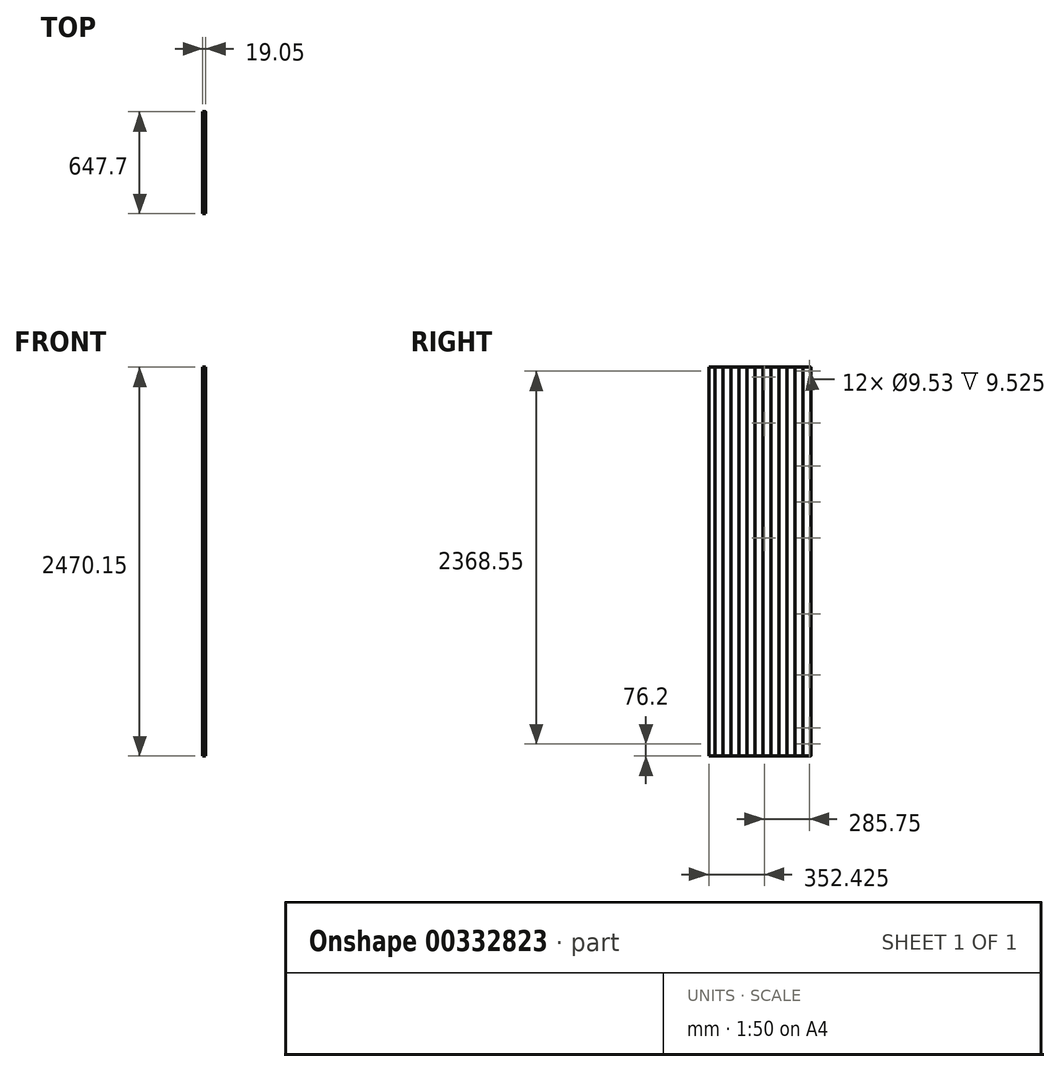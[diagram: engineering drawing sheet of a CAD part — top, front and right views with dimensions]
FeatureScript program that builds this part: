
annotation { "Feature Type Name" : "Feature", "Feature Type Description" : "" }
export const myFeature = defineFeature(function(context is Context, id is Id, definition is map)
    precondition{}
    {
        {
            var Q0;
            Q0=qCreatedBy(makeId("Right.planeOp"),FACE);
            var sketch = newSketch(context, id + "F0", { "sketchPlane" : qUnion([Q0])});
            skLineSegment(sketch, "E0.bottom", {"start": v(0, 0) * mm, "end": v(-647.7, 0) * mm});
            skLineSegment(sketch, "E0.top", {"start": v(0, 2470.15) * mm, "end": v(-647.7, 2470.15) * mm});
            skLineSegment(sketch, "E0.left", {"start": v(0, 0) * mm, "end": v(0, 2470.15) * mm});
            skLineSegment(sketch, "E0.right", {"start": v(-647.7, 0) * mm, "end": v(-647.7, 2470.15) * mm});
            skSolve(sketch);
        }
        {
            var Q0;
            Q0=qSketchRegion(id+"F0",true);
            extrude(context, id + "F1", {"entities" : qUnion([Q0]), "depth" : 19.05 * mm});
        }
        {
            var Q0;
            Q0=qCreatedBy(makeId("Right.planeOp"),FACE);
            cPlane(context, id + "F2", {"entities" : qUnion([Q0]), "cplaneType" : CPlaneType.OFFSET, "offset" : 25.4 * mm, "oppositeDirection" : true, "width" : 152.4 * mm, "height" : 152.4 * mm});
        }
        {
            var Q0;
            Q0=qCreatedBy(id+"F2.planeOp",FACE);
            var sketch = newSketch(context, id + "F3", { "sketchPlane" : qUnion([Q0])});
            skCircle(sketch, "E1", {"center": v(-536.58, 63.5) * mm, "radius": 4.76 * mm, "construction": true});
            skCircle(sketch, "E2", {"center": v(-9.52, 76.2) * mm, "radius": 4.76 * mm});
            skCircle(sketch, "E3", {"center": v(-536.58, 177.8) * mm, "radius": 4.76 * mm, "construction": true});
            skCircle(sketch, "E4", {"center": v(-600.08, 177.8) * mm, "radius": 4.76 * mm, "construction": true});
            skCircle(sketch, "E5", {"center": v(-600.07, 901.7) * mm, "radius": 4.76 * mm, "construction": true});
            skCircle(sketch, "E6", {"center": v(-295.28, 1384.3) * mm, "radius": 4.76 * mm});
            skCircle(sketch, "E7", {"center": v(-295.28, 2114.55) * mm, "radius": 4.76 * mm});
            skCircle(sketch, "E8", {"center": v(-295.28, 2406.65) * mm, "radius": 4.76 * mm});
            skCircle(sketch, "E9", {"center": v(-9.53, 2444.75) * mm, "radius": 4.76 * mm});
            skCircle(sketch, "E10", {"center": v(-9.53, 2114.55) * mm, "radius": 4.76 * mm});
            skCircle(sketch, "E11", {"center": v(-9.53, 1384.3) * mm, "radius": 4.76 * mm});
            skCircle(sketch, "E12", {"center": v(-9.53, 901.7) * mm, "radius": 4.76 * mm});
            skCircle(sketch, "E13", {"center": v(-9.53, 177.8) * mm, "radius": 4.76 * mm});
            skCircle(sketch, "E14", {"center": v(-536.58, 76.2) * mm, "radius": 4.76 * mm, "construction": true});
            skCircle(sketch, "E15", {"center": v(-558.8, 161.93) * mm, "radius": 4.76 * mm, "construction": true});
            skCircle(sketch, "E16", {"center": v(-600.08, 514.35) * mm, "radius": 4.76 * mm, "construction": true});
            skCircle(sketch, "E17", {"center": v(-9.53, 514.35) * mm, "radius": 4.76 * mm});
            skCircle(sketch, "E18", {"center": v(-9.53, 1612.9) * mm, "radius": 4.76 * mm});
            skCircle(sketch, "E19", {"center": v(-9.53, 1841.5) * mm, "radius": 4.76 * mm});
            skSolve(sketch);
        }
        {
            var Q0;
            Q0=qSketchRegion(id+"F3",true);
            extrude(context, id + "F4", {"entities" : qUnion([Q0]), "operationType" : NewBodyOperationType.REMOVE, "depth" : 34.92 * mm});
        }
        {
            var Q0;
            Q0=qCreatedBy(makeId("Top.planeOp"),FACE);
            var sketch = newSketch(context, id + "F5", { "sketchPlane" : qUnion([Q0])});
            skArc(sketch, "E20", {"start": v(19.05, 50.3) * mm, "mid": v(18.9, 50.65) * mm, "end": v(18.54, 50.8) * mm});
            skArc(sketch, "E21", {"start": v(18.54, 50.8) * mm, "mid": v(18.9, 50.95) * mm, "end": v(19.05, 51.3) * mm});
            skArc(sketch, "E22", {"start": v(19.05, 50.3) * mm, "mid": v(19.56, 50.8) * mm, "end": v(19.05, 51.3) * mm});
            skLineSegment(sketch, "E23", {"start": v(19.05, 50.8) * mm, "end": v(19.05, 48.26) * mm});
            skArc(sketch, "E24.1.0.0", {"start": v(19.05, -0.5) * mm, "mid": v(19.56, 0) * mm, "end": v(19.05, 0.5) * mm});
            skLineSegment(sketch, "E24.1.0.1", {"start": v(19.05, 0) * mm, "end": v(19.05, -2.54) * mm});
            skArc(sketch, "E24.1.0.2", {"start": v(19.05, -0.5) * mm, "mid": v(18.9, -0.15) * mm, "end": v(18.54, 0) * mm});
            skArc(sketch, "E24.1.0.3", {"start": v(18.54, 0) * mm, "mid": v(18.9, 0.15) * mm, "end": v(19.05, 0.5) * mm});
            skArc(sketch, "E24.2.0.0", {"start": v(19.05, -51.3) * mm, "mid": v(19.56, -50.8) * mm, "end": v(19.05, -50.3) * mm});
            skLineSegment(sketch, "E24.2.0.1", {"start": v(19.05, -50.8) * mm, "end": v(19.05, -53.34) * mm});
            skArc(sketch, "E24.2.0.2", {"start": v(19.05, -51.3) * mm, "mid": v(18.9, -50.95) * mm, "end": v(18.54, -50.8) * mm});
            skArc(sketch, "E24.2.0.3", {"start": v(18.54, -50.8) * mm, "mid": v(18.9, -50.65) * mm, "end": v(19.05, -50.3) * mm});
            skArc(sketch, "E24.3.0.0", {"start": v(19.05, -102.1) * mm, "mid": v(19.56, -101.6) * mm, "end": v(19.05, -101.1) * mm});
            skLineSegment(sketch, "E24.3.0.1", {"start": v(19.05, -101.6) * mm, "end": v(19.05, -104.14) * mm});
            skArc(sketch, "E24.3.0.2", {"start": v(19.05, -102.1) * mm, "mid": v(18.9, -101.75) * mm, "end": v(18.54, -101.6) * mm});
            skArc(sketch, "E24.3.0.3", {"start": v(18.54, -101.6) * mm, "mid": v(18.9, -101.45) * mm, "end": v(19.05, -101.1) * mm});
            skArc(sketch, "E24.4.0.0", {"start": v(19.05, -152.9) * mm, "mid": v(19.56, -152.4) * mm, "end": v(19.05, -151.9) * mm});
            skLineSegment(sketch, "E24.4.0.1", {"start": v(19.05, -152.4) * mm, "end": v(19.05, -154.94) * mm});
            skArc(sketch, "E24.4.0.2", {"start": v(19.05, -152.9) * mm, "mid": v(18.9, -152.55) * mm, "end": v(18.54, -152.4) * mm});
            skArc(sketch, "E24.4.0.3", {"start": v(18.54, -152.4) * mm, "mid": v(18.9, -152.25) * mm, "end": v(19.05, -151.9) * mm});
            skArc(sketch, "E24.5.0.0", {"start": v(19.05, -203.7) * mm, "mid": v(19.56, -203.2) * mm, "end": v(19.05, -202.7) * mm});
            skLineSegment(sketch, "E24.5.0.1", {"start": v(19.05, -203.2) * mm, "end": v(19.05, -205.74) * mm});
            skArc(sketch, "E24.5.0.2", {"start": v(19.05, -203.7) * mm, "mid": v(18.9, -203.35) * mm, "end": v(18.54, -203.2) * mm});
            skArc(sketch, "E24.5.0.3", {"start": v(18.54, -203.2) * mm, "mid": v(18.9, -203.05) * mm, "end": v(19.05, -202.7) * mm});
            skArc(sketch, "E24.6.0.0", {"start": v(19.05, -254.5) * mm, "mid": v(19.56, -254) * mm, "end": v(19.05, -253.5) * mm});
            skLineSegment(sketch, "E24.6.0.1", {"start": v(19.05, -254) * mm, "end": v(19.05, -256.54) * mm});
            skArc(sketch, "E24.6.0.2", {"start": v(19.05, -254.5) * mm, "mid": v(18.9, -254.15) * mm, "end": v(18.54, -254) * mm});
            skArc(sketch, "E24.6.0.3", {"start": v(18.54, -254) * mm, "mid": v(18.9, -253.85) * mm, "end": v(19.05, -253.5) * mm});
            skArc(sketch, "E24.7.0.0", {"start": v(19.05, -305.3) * mm, "mid": v(19.56, -304.8) * mm, "end": v(19.05, -304.3) * mm});
            skLineSegment(sketch, "E24.7.0.1", {"start": v(19.05, -304.8) * mm, "end": v(19.05, -307.34) * mm});
            skArc(sketch, "E24.7.0.2", {"start": v(19.05, -305.3) * mm, "mid": v(18.9, -304.95) * mm, "end": v(18.54, -304.8) * mm});
            skArc(sketch, "E24.7.0.3", {"start": v(18.54, -304.8) * mm, "mid": v(18.9, -304.65) * mm, "end": v(19.05, -304.3) * mm});
            skArc(sketch, "E24.8.0.0", {"start": v(19.05, -356.1) * mm, "mid": v(19.56, -355.6) * mm, "end": v(19.05, -355.1) * mm});
            skLineSegment(sketch, "E24.8.0.1", {"start": v(19.05, -355.6) * mm, "end": v(19.05, -358.14) * mm});
            skArc(sketch, "E24.8.0.2", {"start": v(19.05, -356.1) * mm, "mid": v(18.9, -355.75) * mm, "end": v(18.54, -355.6) * mm});
            skArc(sketch, "E24.8.0.3", {"start": v(18.54, -355.6) * mm, "mid": v(18.9, -355.45) * mm, "end": v(19.05, -355.1) * mm});
            skArc(sketch, "E24.9.0.0", {"start": v(19.05, -406.9) * mm, "mid": v(19.56, -406.4) * mm, "end": v(19.05, -405.9) * mm});
            skLineSegment(sketch, "E24.9.0.1", {"start": v(19.05, -406.4) * mm, "end": v(19.05, -408.94) * mm});
            skArc(sketch, "E24.9.0.2", {"start": v(19.05, -406.9) * mm, "mid": v(18.9, -406.55) * mm, "end": v(18.54, -406.4) * mm});
            skArc(sketch, "E24.9.0.3", {"start": v(18.54, -406.4) * mm, "mid": v(18.9, -406.25) * mm, "end": v(19.05, -405.9) * mm});
            skArc(sketch, "E24.10.0.0", {"start": v(19.05, -457.7) * mm, "mid": v(19.56, -457.2) * mm, "end": v(19.05, -456.7) * mm});
            skLineSegment(sketch, "E24.10.0.1", {"start": v(19.05, -457.2) * mm, "end": v(19.05, -459.74) * mm});
            skArc(sketch, "E24.10.0.2", {"start": v(19.05, -457.7) * mm, "mid": v(18.9, -457.35) * mm, "end": v(18.54, -457.2) * mm});
            skArc(sketch, "E24.10.0.3", {"start": v(18.54, -457.2) * mm, "mid": v(18.9, -457.05) * mm, "end": v(19.05, -456.7) * mm});
            skArc(sketch, "E24.11.0.0", {"start": v(19.05, -508.5) * mm, "mid": v(19.56, -508) * mm, "end": v(19.05, -507.5) * mm});
            skLineSegment(sketch, "E24.11.0.1", {"start": v(19.05, -508) * mm, "end": v(19.05, -510.54) * mm});
            skArc(sketch, "E24.11.0.2", {"start": v(19.05, -508.5) * mm, "mid": v(18.9, -508.15) * mm, "end": v(18.54, -508) * mm});
            skArc(sketch, "E24.11.0.3", {"start": v(18.54, -508) * mm, "mid": v(18.9, -507.85) * mm, "end": v(19.05, -507.5) * mm});
            skArc(sketch, "E24.12.0.0", {"start": v(19.05, -559.3) * mm, "mid": v(19.56, -558.8) * mm, "end": v(19.05, -558.3) * mm});
            skLineSegment(sketch, "E24.12.0.1", {"start": v(19.05, -558.8) * mm, "end": v(19.05, -561.34) * mm});
            skArc(sketch, "E24.12.0.2", {"start": v(19.05, -559.3) * mm, "mid": v(18.9, -558.95) * mm, "end": v(18.54, -558.8) * mm});
            skArc(sketch, "E24.12.0.3", {"start": v(18.54, -558.8) * mm, "mid": v(18.9, -558.65) * mm, "end": v(19.05, -558.3) * mm});
            skArc(sketch, "E24.13.0.0", {"start": v(19.05, -610.1) * mm, "mid": v(19.56, -609.6) * mm, "end": v(19.05, -609.1) * mm});
            skLineSegment(sketch, "E24.13.0.1", {"start": v(19.05, -609.6) * mm, "end": v(19.05, -612.14) * mm});
            skArc(sketch, "E24.13.0.2", {"start": v(19.05, -610.1) * mm, "mid": v(18.9, -609.75) * mm, "end": v(18.54, -609.6) * mm});
            skArc(sketch, "E24.13.0.3", {"start": v(18.54, -609.6) * mm, "mid": v(18.9, -609.45) * mm, "end": v(19.05, -609.1) * mm});
            skArc(sketch, "E24.14.0.0", {"start": v(19.05, -660.9) * mm, "mid": v(19.56, -660.4) * mm, "end": v(19.05, -659.9) * mm});
            skArc(sketch, "E24.14.0.2", {"start": v(19.05, -660.9) * mm, "mid": v(18.9, -660.55) * mm, "end": v(18.54, -660.4) * mm});
            skArc(sketch, "E24.14.0.3", {"start": v(18.54, -660.4) * mm, "mid": v(18.9, -660.25) * mm, "end": v(19.05, -659.9) * mm});
            skArc(sketch, "E24.15.0.0", {"start": v(19.05, -711.7) * mm, "mid": v(19.56, -711.2) * mm, "end": v(19.05, -710.7) * mm});
            skLineSegment(sketch, "E24.15.0.1", {"start": v(19.05, -711.2) * mm, "end": v(19.05, -713.74) * mm});
            skArc(sketch, "E24.15.0.2", {"start": v(19.05, -711.7) * mm, "mid": v(18.9, -711.35) * mm, "end": v(18.54, -711.2) * mm});
            skArc(sketch, "E24.15.0.3", {"start": v(18.54, -711.2) * mm, "mid": v(18.9, -711.05) * mm, "end": v(19.05, -710.7) * mm});
            skLineSegment(sketch, "E24.direction1", {"start": v(19.05, 48.26) * mm, "end": v(19.05, -2.54) * mm, "construction": true});
            skSolve(sketch);
        }
        {
            var Q0;
            Q0 = qSketchRegion(id + "F5", true);
            extrude(context, id + "F6", {"entities" : qUnion([Q0]), "operationType" : NewBodyOperationType.REMOVE, "depth" : 2540 * mm});
        }
    });
